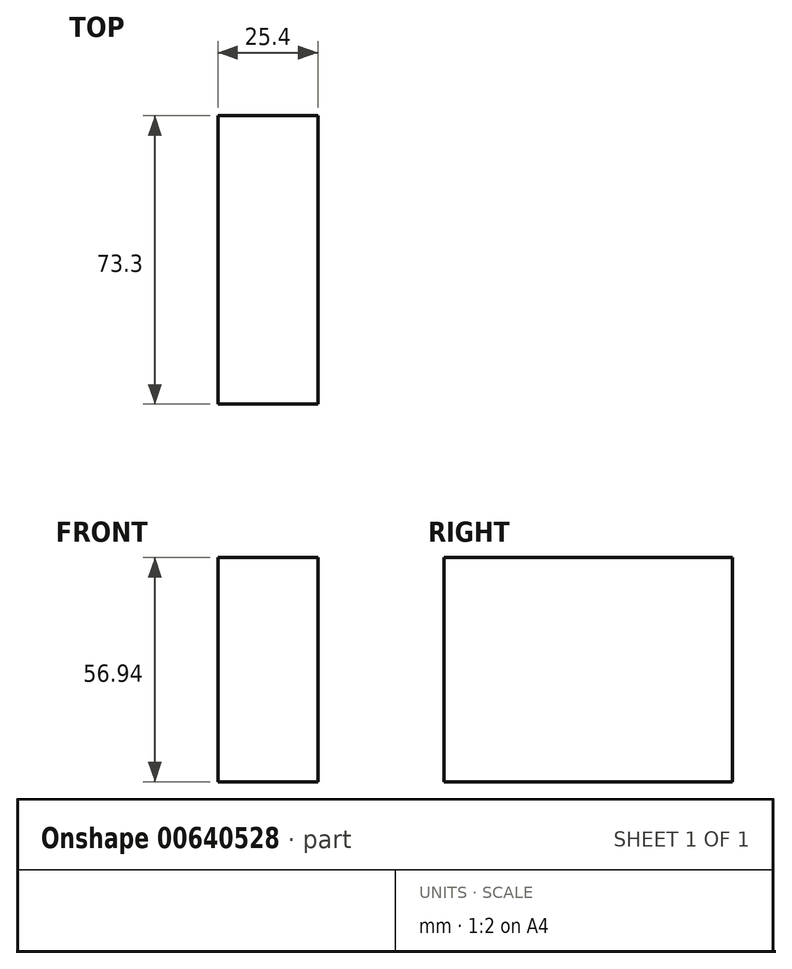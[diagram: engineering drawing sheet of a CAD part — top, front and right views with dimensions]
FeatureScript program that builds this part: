
annotation { "Feature Type Name" : "Feature", "Feature Type Description" : "" }
export const myFeature = defineFeature(function(context is Context, id is Id, definition is map)
    precondition{}
    {
        {
            var Q0;
            Q0=qCreatedBy(makeId("Right.planeOp"),FACE);
            var sketch = newSketch(context, id + "F0", { "sketchPlane" : qUnion([Q0])});
            skLineSegment(sketch, "E0.bottom", {"start": v(36.65, 28.47) * mm, "end": v(-36.65, 28.47) * mm});
            skLineSegment(sketch, "E0.top", {"start": v(36.65, -28.47) * mm, "end": v(-36.65, -28.47) * mm});
            skLineSegment(sketch, "E0.left", {"start": v(36.65, 28.47) * mm, "end": v(36.65, -28.47) * mm});
            skLineSegment(sketch, "E0.right", {"start": v(-36.65, 28.47) * mm, "end": v(-36.65, -28.47) * mm});
            skPoint(sketch, "E0.middle", {"position": v(0, 0) * mm});
            skSolve(sketch);
        }
        {
            var Q0;
            Q0=makeQuery(id+"F0.imprint","IMPRINT",FACE,{"disambiguationData":[TD([[makeQuery(id+"F0.imprint","IMPRINT",EDGE,{"derivedFrom":sQuery(id+"F0.wireOp",EDGE,"E0.bottom")}),1.0]])]});
            extrude(context, id + "F1", {"entities" : qUnion([Q0]), "endBound" : BoundingType.SYMMETRIC, "depth" : 25.4 * mm, "offsetDistance" : 25.4 * mm});
        }
    });
